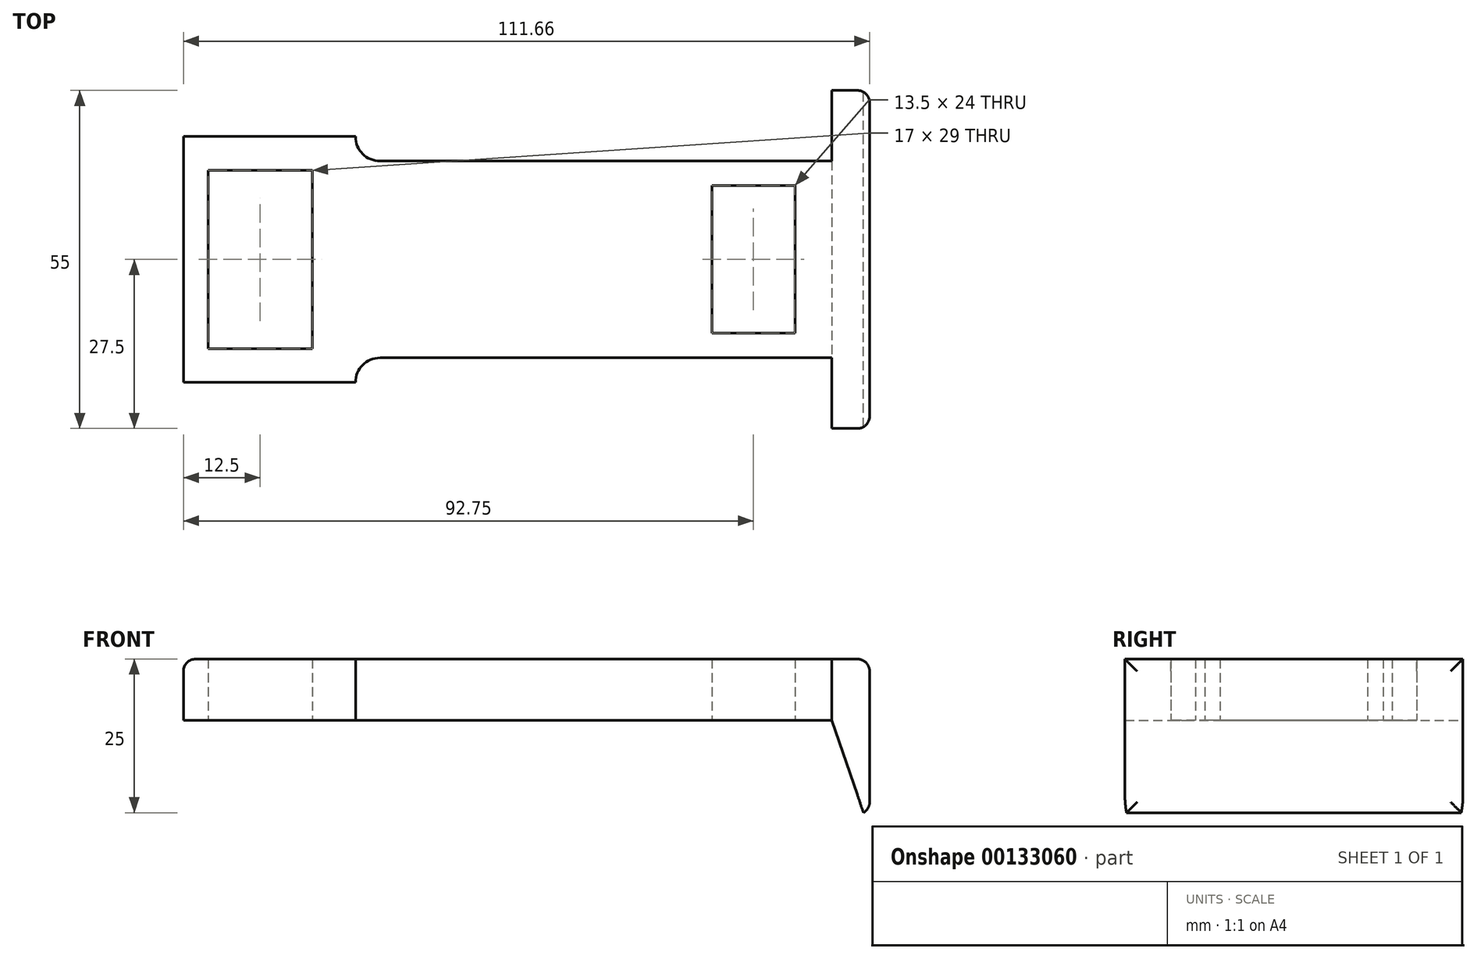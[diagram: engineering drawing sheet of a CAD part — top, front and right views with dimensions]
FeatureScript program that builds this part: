
annotation { "Feature Type Name" : "Feature", "Feature Type Description" : "" }
export const myFeature = defineFeature(function(context is Context, id is Id, definition is map)
    precondition{}
    {
        {
            var Q0;
            Q0=qCreatedBy(makeId("Top.planeOp"),FACE);
            var sketch = newSketch(context, id + "F0", { "sketchPlane" : qUnion([Q0])});
            skLineSegment(sketch, "E0", {"start": v(0, 0) * mm, "end": v(0, 20) * mm});
            skLineSegment(sketch, "E1", {"start": v(0, 20) * mm, "end": v(28, 20) * mm});
            skLineSegment(sketch, "E2", {"start": v(28, 20) * mm, "end": v(28, 20) * mm});
            skLineSegment(sketch, "E3", {"start": v(4, 0) * mm, "end": v(4, 14.5) * mm});
            skLineSegment(sketch, "E4", {"start": v(4, 14.5) * mm, "end": v(21, 14.5) * mm});
            skLineSegment(sketch, "E5", {"start": v(21, 14.5) * mm, "end": v(21, 0) * mm});
            skLineSegment(sketch, "E6.MirrorCS", {"start": v(0, 0) * mm, "end": v(0, -20) * mm});
            skLineSegment(sketch, "E7.MirrorCS", {"start": v(0, -20) * mm, "end": v(28, -20) * mm});
            skLineSegment(sketch, "E8.MirrorCS", {"start": v(28, -20) * mm, "end": v(28, -20) * mm});
            skLineSegment(sketch, "E9.MirrorCS", {"start": v(105.5, 0) * mm, "end": v(105.5, 0) * mm});
            skLineSegment(sketch, "E10.MirrorCS", {"start": v(21, -14.5) * mm, "end": v(21, 0) * mm});
            skLineSegment(sketch, "E11.MirrorCS", {"start": v(4, -14.5) * mm, "end": v(21, -14.5) * mm});
            skLineSegment(sketch, "E12.MirrorCS", {"start": v(4, 0) * mm, "end": v(4, -14.5) * mm});
            skPoint(sketch, "E13.visualSharp", {"position": v(28, 16) * mm});
            skArc(sketch, "E13.filletArc", {"start": v(28, 20) * mm, "mid": v(29.17, 17.17) * mm, "end": v(32, 16) * mm});
            skPoint(sketch, "E14.visualSharp", {"position": v(28, -16) * mm});
            skArc(sketch, "E14.filletArc", {"start": v(32, -16) * mm, "mid": v(29.17, -17.17) * mm, "end": v(28, -20) * mm});
            skLineSegment(sketch, "E15", {"start": v(32, 16) * mm, "end": v(105.5, 16) * mm});
            skLineSegment(sketch, "E16", {"start": v(105.5, 16) * mm, "end": v(105.5, -16) * mm});
            skLineSegment(sketch, "E17", {"start": v(105.5, -16) * mm, "end": v(32, -16) * mm});
            skLineSegment(sketch, "E18.bottom", {"start": v(99.5, -12) * mm, "end": v(86, -12) * mm});
            skLineSegment(sketch, "E18.top", {"start": v(99.5, 12) * mm, "end": v(86, 12) * mm});
            skLineSegment(sketch, "E18.left", {"start": v(99.5, -12) * mm, "end": v(99.5, 12) * mm});
            skLineSegment(sketch, "E18.right", {"start": v(86, -12) * mm, "end": v(86, 12) * mm});
            skSolve(sketch);
        }
        {
            var Q0;
            Q0 = qSketchRegion(id + "F0", true);
            extrude(context, id + "F1", {"entities" : qUnion([Q0]), "depth" : 10 * mm});
        }
        {
            var Q0;
            Q0=qCreatedBy(makeId("Front.planeOp"),FACE);
            var sketch = newSketch(context, id + "F2", { "sketchPlane" : qUnion([Q0])});
            skLineSegment(sketch, "E19", {"start": v(105.5, 0) * mm, "end": v(110.66, -15) * mm});
            skLineSegment(sketch, "E20", {"start": v(105.5, 0) * mm, "end": v(105.5, 10) * mm});
            skLineSegment(sketch, "E21", {"start": v(110.66, -15) * mm, "end": v(111.66, -15) * mm});
            skLineSegment(sketch, "E22", {"start": v(111.66, -15) * mm, "end": v(111.66, 10) * mm});
            skLineSegment(sketch, "E23", {"start": v(105.5, 10) * mm, "end": v(111.66, 10) * mm});
            skSolve(sketch);
        }
        {
            var Q0;
            Q0 = qSketchRegion(id + "F2", true);
            extrude(context, id + "F3", {"entities" : qUnion([Q0]), "operationType" : NewBodyOperationType.ADD, "flatOperationType" : FlatOperationType.REMOVE, "endBound" : BoundingType.SYMMETRIC, "offsetDistance" : 25 * mm, "depth" : 55 * mm, "domain" : OperationDomain.MODEL});
        }
        {
            var Q0;
            Q0=makeQuery(id+"F3.opExtrude","SWEPT_FACE",FACE,{"disambiguationData":[OSD([sQuery(id+"F2.wireOp",EDGE,"E22")])]});
            fillet(context, id + "F4", {"entities" : qUnion([Q0]), "radius" : 2 * mm, "tangentPropagation" : true, "allowEdgeOverflow" : false});
        }
        {
            var Q0;
            Q0=makeQuery(id+"F1.opExtrude","CAP_EDGE",EDGE,{"disambiguationData":[OSD([sQuery(id+"F0.wireOp",EDGE,"E0"),sQuery(id+"F0.wireOp",EDGE,"E6.MirrorCS")])],"isStart":false});
            fillet(context, id + "F5", {"entities" : qUnion([Q0]), "radius" : 2 * mm, "tangentPropagation" : true, "allowEdgeOverflow" : false});
        }
    });
